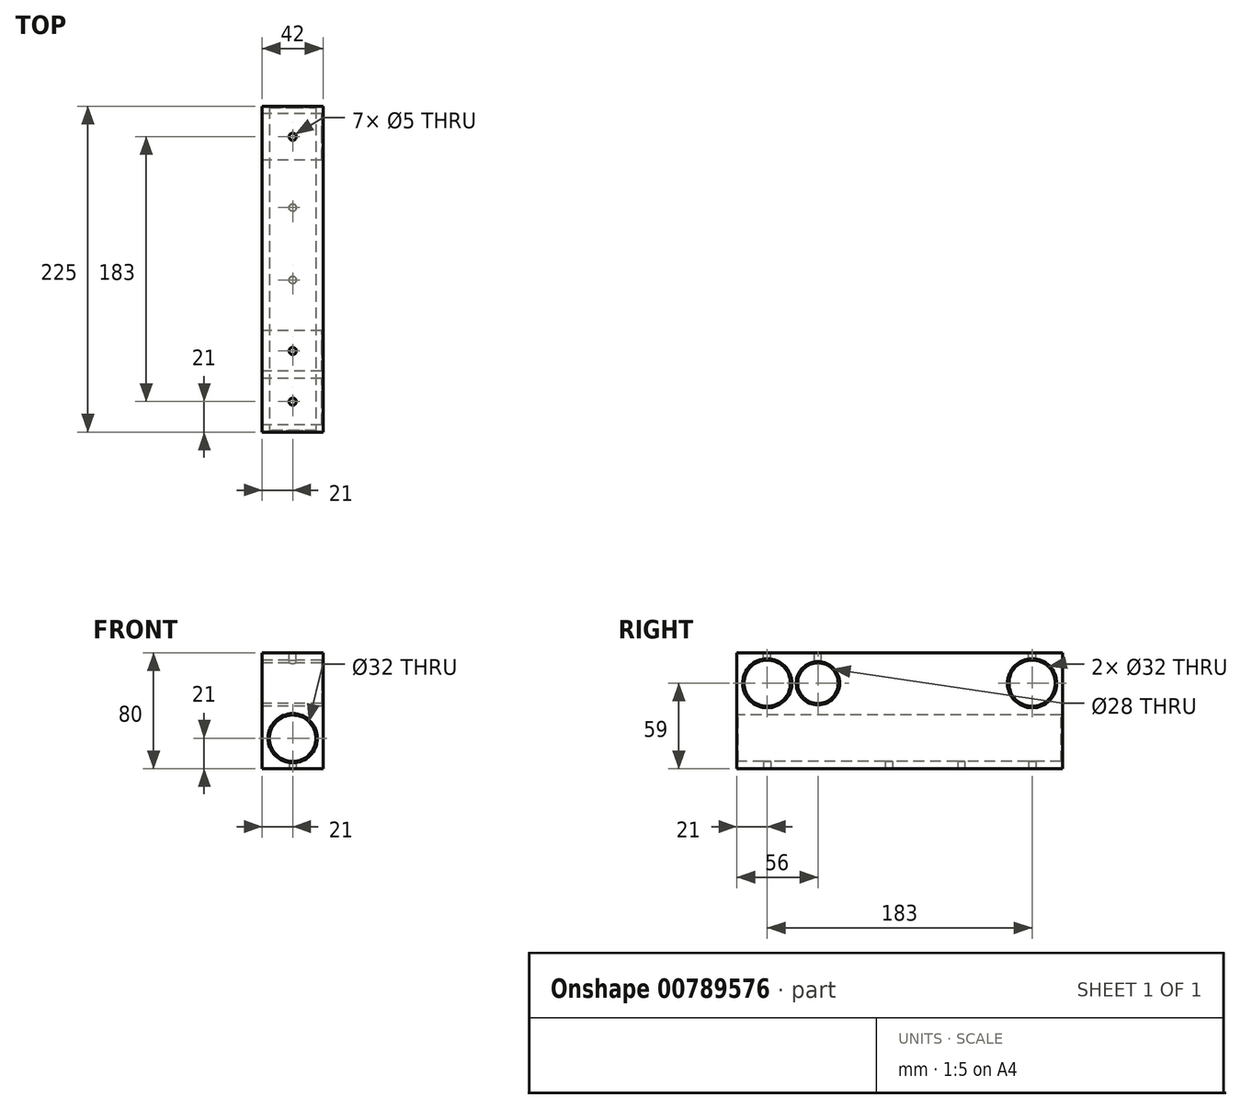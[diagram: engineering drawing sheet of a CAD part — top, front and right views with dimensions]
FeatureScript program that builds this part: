
annotation { "Feature Type Name" : "Feature", "Feature Type Description" : "" }
export const myFeature = defineFeature(function(context is Context, id is Id, definition is map)
    precondition{}
    {
        {
            var Q0;
            Q0=qCreatedBy(makeId("Front.planeOp"),FACE);
            var sketch = newSketch(context, id + "F0", { "sketchPlane" : qUnion([Q0])});
            skLineSegment(sketch, "E0.bottom", {"start": v(-21, 40) * mm, "end": v(21, 40) * mm});
            skLineSegment(sketch, "E0.top", {"start": v(-21, -40) * mm, "end": v(21, -40) * mm});
            skLineSegment(sketch, "E0.left", {"start": v(-21, 40) * mm, "end": v(-21, -40) * mm});
            skLineSegment(sketch, "E0.right", {"start": v(21, 40) * mm, "end": v(21, -40) * mm});
            skPoint(sketch, "E0.middle", {"position": v(0, 0) * mm});
            skPoint(sketch, "E1", {"position": v(0, -19) * mm});
            skCircle(sketch, "E2", {"center": v(0, -19) * mm, "radius": 16 * mm});
            skSolve(sketch);
        }
        {
            var Q0;
            Q0=makeQuery(id+"F0.imprint","IMPRINT",FACE,{"disambiguationData":[TD([[makeQuery(id+"F0.imprint","IMPRINT",EDGE,{"derivedFrom":sQuery(id+"F0.wireOp",EDGE,"E0.bottom")}),-1.0]])]});
            extrude(context, id + "F1", {"entities" : qUnion([Q0]), "oppositeDirection" : true, "depth" : 225 * mm, "offsetDistance" : 25 * mm});
        }
        {
            var Q0;
            Q0=makeQuery(id+"F1.opExtrude","SWEPT_FACE",FACE,{"disambiguationData":[OSD([sQuery(id+"F0.wireOp",EDGE,"E0.left")])]});
            var sketch = newSketch(context, id + "F2", { "sketchPlane" : qUnion([Q0])});
            skPoint(sketch, "E3", {"position": v(-21, 19) * mm});
            skPoint(sketch, "E4", {"position": v(-56, 19) * mm});
            skPoint(sketch, "E5", {"position": v(-204, 19) * mm});
            skCircle(sketch, "E6", {"center": v(-21, 19) * mm, "radius": 16 * mm});
            skCircle(sketch, "E7", {"center": v(-56, 19) * mm, "radius": 14 * mm});
            skCircle(sketch, "E8", {"center": v(-204, 19) * mm, "radius": 16 * mm});
            skSolve(sketch);
        }
        {
            var Q0;
            Q0=makeQuery(id+"F2.imprint","IMPRINT",FACE,{"disambiguationData":[TD([[makeQuery(id+"F2.imprint","IMPRINT",EDGE,{"derivedFrom":sQuery(id+"F2.wireOp",EDGE,"E8")}),1.0]])]});
            var Q1;
            Q1=makeQuery(id+"F2.imprint","IMPRINT",FACE,{"disambiguationData":[TD([[makeQuery(id+"F2.imprint","IMPRINT",EDGE,{"derivedFrom":sQuery(id+"F2.wireOp",EDGE,"E7")}),1.0]])]});
            var Q2;
            Q2=makeQuery(id+"F2.imprint","IMPRINT",FACE,{"disambiguationData":[TD([[makeQuery(id+"F2.imprint","IMPRINT",EDGE,{"derivedFrom":sQuery(id+"F2.wireOp",EDGE,"E6")}),1.0]])]});
            extrude(context, id + "F3", {"entities" : qUnion([Q0, Q1, Q2]), "operationType" : NewBodyOperationType.REMOVE, "oppositeDirection" : true, "depth" : 100 * mm, "offsetDistance" : 25 * mm});
        }
        {
            var Q0;
            Q0=makeQuery(id+"F1.opExtrude","SWEPT_FACE",FACE,{"disambiguationData":[OSD([sQuery(id+"F0.wireOp",EDGE,"E0.bottom")])]});
            var sketch = newSketch(context, id + "F4", { "sketchPlane" : qUnion([Q0])});
            skPoint(sketch, "E9", {"position": v(0, 21) * mm});
            skPoint(sketch, "E10", {"position": v(0, 56) * mm});
            skPoint(sketch, "E11", {"position": v(0, 204) * mm});
            skCircle(sketch, "E12", {"center": v(0, 21) * mm, "radius": 2.5 * mm});
            skCircle(sketch, "E13", {"center": v(0, 56) * mm, "radius": 2.5 * mm});
            skCircle(sketch, "E14", {"center": v(0, 204) * mm, "radius": 2.5 * mm});
            skSolve(sketch);
        }
        {
            var Q0;
            Q0=makeQuery(id+"F4.imprint","IMPRINT",FACE,{"disambiguationData":[TD([[makeQuery(id+"F4.imprint","IMPRINT",EDGE,{"derivedFrom":sQuery(id+"F4.wireOp",EDGE,"E12")}),1.0]])]});
            var Q1;
            Q1=makeQuery(id+"F4.imprint","IMPRINT",FACE,{"disambiguationData":[TD([[makeQuery(id+"F4.imprint","IMPRINT",EDGE,{"derivedFrom":sQuery(id+"F4.wireOp",EDGE,"E13")}),1.0]])]});
            var Q2;
            Q2=makeQuery(id+"F4.imprint","IMPRINT",FACE,{"disambiguationData":[TD([[makeQuery(id+"F4.imprint","IMPRINT",EDGE,{"derivedFrom":sQuery(id+"F4.wireOp",EDGE,"E14")}),1.0]])]});
            extrude(context, id + "F5", {"entities" : qUnion([Q0, Q1, Q2]), "operationType" : NewBodyOperationType.REMOVE, "oppositeDirection" : true, "depth" : 25 * mm, "offsetDistance" : 25 * mm});
        }
        {
            var Q0;
            Q0=makeQuery(id+"F1.opExtrude","SWEPT_FACE",FACE,{"disambiguationData":[OSD([sQuery(id+"F0.wireOp",EDGE,"E0.top")])]});
            var sketch = newSketch(context, id + "F6", { "sketchPlane" : qUnion([Q0])});
            skPoint(sketch, "E15", {"position": v(0, -21) * mm});
            skPoint(sketch, "E16", {"position": v(0, -204) * mm});
            skCircle(sketch, "E17", {"center": v(0, -21) * mm, "radius": 2.5 * mm});
            skCircle(sketch, "E18", {"center": v(0, -204) * mm, "radius": 2.5 * mm});
            skPoint(sketch, "E19", {"position": v(0, -130) * mm});
            skPoint(sketch, "E20", {"position": v(0, -105) * mm});
            skPoint(sketch, "E21", {"position": v(0, -155) * mm});
            skCircle(sketch, "E22", {"center": v(0, -105) * mm, "radius": 2.5 * mm});
            skCircle(sketch, "E23", {"center": v(0, -155) * mm, "radius": 2.5 * mm});
            skSolve(sketch);
        }
        {
            var Q0;
            Q0 = qSketchRegion(id + "F6", true);
            extrude(context, id + "F7", {"entities" : qUnion([Q0]), "operationType" : NewBodyOperationType.REMOVE, "oppositeDirection" : true, "depth" : 25 * mm, "offsetDistance" : 25 * mm});
        }
        {
            var Q0;
            Q0=makeQuery(id+"F3.boolean.opBoolean","COPY",EDGE,{"derivedFrom":makeQuery(id+"F3.opExtrude","CAP_EDGE",EDGE,{"disambiguationData":[OSD([sQuery(id+"F2.wireOp",EDGE,"E7")])],"isStart":true})});
            var Q1;
            Q1=makeQuery(id+"F3.boolean.opBoolean","COPY",EDGE,{"derivedFrom":makeQuery(id+"F3.opExtrude","CAP_EDGE",EDGE,{"disambiguationData":[OSD([sQuery(id+"F2.wireOp",EDGE,"E6")])],"isStart":true})});
            var Q2;
            Q2=makeQuery(id+"F1.opExtrude","CAP_EDGE",EDGE,{"disambiguationData":[OSD([sQuery(id+"F0.wireOp",EDGE,"E2")])],"isStart":true});
            var Q3;
            Q3=makeQuery(id+"F3.boolean.opBoolean","COPY",EDGE,{"derivedFrom":makeQuery(id+"F3.opExtrude","CAP_EDGE",EDGE,{"disambiguationData":[OSD([sQuery(id+"F2.wireOp",EDGE,"E8")])],"isStart":true})});
            var Q4;
            Q4=makeQuery(id+"F3.boolean.opBoolean","INTERSECT",EDGE,{"derivedFrom":[makeQuery(id+"F1.opExtrude","SWEPT_FACE",FACE,{"disambiguationData":[OSD([sQuery(id+"F0.wireOp",EDGE,"E0.right")])]}),makeQuery(id+"F3.opExtrude","SWEPT_FACE",FACE,{"disambiguationData":[OSD([sQuery(id+"F2.wireOp",EDGE,"E6")])]})]});
            var Q5;
            Q5=makeQuery(id+"F3.boolean.opBoolean","INTERSECT",EDGE,{"derivedFrom":[makeQuery(id+"F1.opExtrude","SWEPT_FACE",FACE,{"disambiguationData":[OSD([sQuery(id+"F0.wireOp",EDGE,"E0.right")])]}),makeQuery(id+"F3.opExtrude","SWEPT_FACE",FACE,{"disambiguationData":[OSD([sQuery(id+"F2.wireOp",EDGE,"E7")])]})]});
            var Q6;
            Q6=makeQuery(id+"F3.boolean.opBoolean","INTERSECT",EDGE,{"derivedFrom":[makeQuery(id+"F1.opExtrude","SWEPT_FACE",FACE,{"disambiguationData":[OSD([sQuery(id+"F0.wireOp",EDGE,"E0.right")])]}),makeQuery(id+"F3.opExtrude","SWEPT_FACE",FACE,{"disambiguationData":[OSD([sQuery(id+"F2.wireOp",EDGE,"E8")])]})]});
            var Q7;
            Q7=makeQuery(id+"F1.opExtrude","CAP_EDGE",EDGE,{"disambiguationData":[OSD([sQuery(id+"F0.wireOp",EDGE,"E2")])],"isStart":false});
            chamfer(context, id + "F8", {"entities" : qUnion([Q0, Q1, Q2, Q3, Q4, Q5, Q6, Q7]), "width" : 1 * mm, "tangentPropagation" : true});
        }
    });
